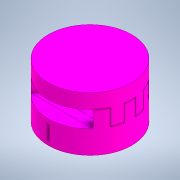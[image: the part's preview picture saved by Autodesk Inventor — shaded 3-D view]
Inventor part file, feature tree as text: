
AUTODESK INVENTOR PART (.ipt)
format: ipt  version: 2020 (Build 240168000, 168)  size: 297,472 bytes
history: native  units: mm
features: extrude x7, sketch x6, draft x2, plane x2, chamfer x1, projected_geometry x1
ambient origin geometry x8: Origin, YZ Plane, XZ Plane, XY Plane, X Axis, Y Axis, Z Axis, Center Point
bodies: Solid1 (feature_tree)
feature tree (19):
  sketch  "Sketch1"  dims[d0=15.0mm d1=10.0mm]
  extrude  "Extrusion1"  Depth=10.0mm
  extrude  "Extrusion2"  Depth=24.0mm TaperAngle=0.0deg
  sketch  "Sketch3"  dims[d5=30.0mm d6=0.0mm d7=7.0mm d8=0.0mm]
  extrude  "Extrusion3"  Depth=7.0mm TaperAngle=0.0deg
  extrude  "Extrusion4"  Depth=7.0mm
  draft  "FaceDraft1"
  draft  "FaceDraft2"
  extrude  "Extrusion5"  Depth=2.0mm TaperAngle=0.0deg
  chamfer  "Chamfer1"  Distance=3.490659mm
  plane  "Work Plane1"
  extrude  "Extrusion6"  Depth=1.0mm
  plane  "Work Plane2"
  extrude  "Extrusion7"  Depth=10.0mm
  sketch  "Sketch2"  dims[d2=40.0mm d3=24.0mm d4=0.0mm]
  projected_geometry  "Projected Loop1"
  sketch  "Sketch4"  dims[d9=11.0mm d10=7.0mm]
  sketch  "Sketch5"  dims[d13=2.0mm d14=0.0mm d15=2.0mm d16=0.0mm]
  sketch  "Sketch6"  dims[d17=3.490659mm d18=3.490659mm d19=1.0mm d20=50.0mm d21=7.0mm d22=2.0mm d23=0.0mm d24=6.4mm d25=2.0mm d26=45.0deg d27=0.2mm d28=0.2mm d29=0.2mm d30=0.2mm d31=0.2mm d32=0.2mm d33=0.2mm d34=4.9mm d35=4.9mm d36=4.9mm d37=4.9mm d38=4.9mm d39=0.0mm d40=0.0mm d41=0.2mm d42=0.2mm d43=0.2mm d44=0.2mm d45=0.2mm d46=0.2mm d47=5.5mm d48=5.5mm d49=5.5mm d50=10.0mm d51=0.0mm]
